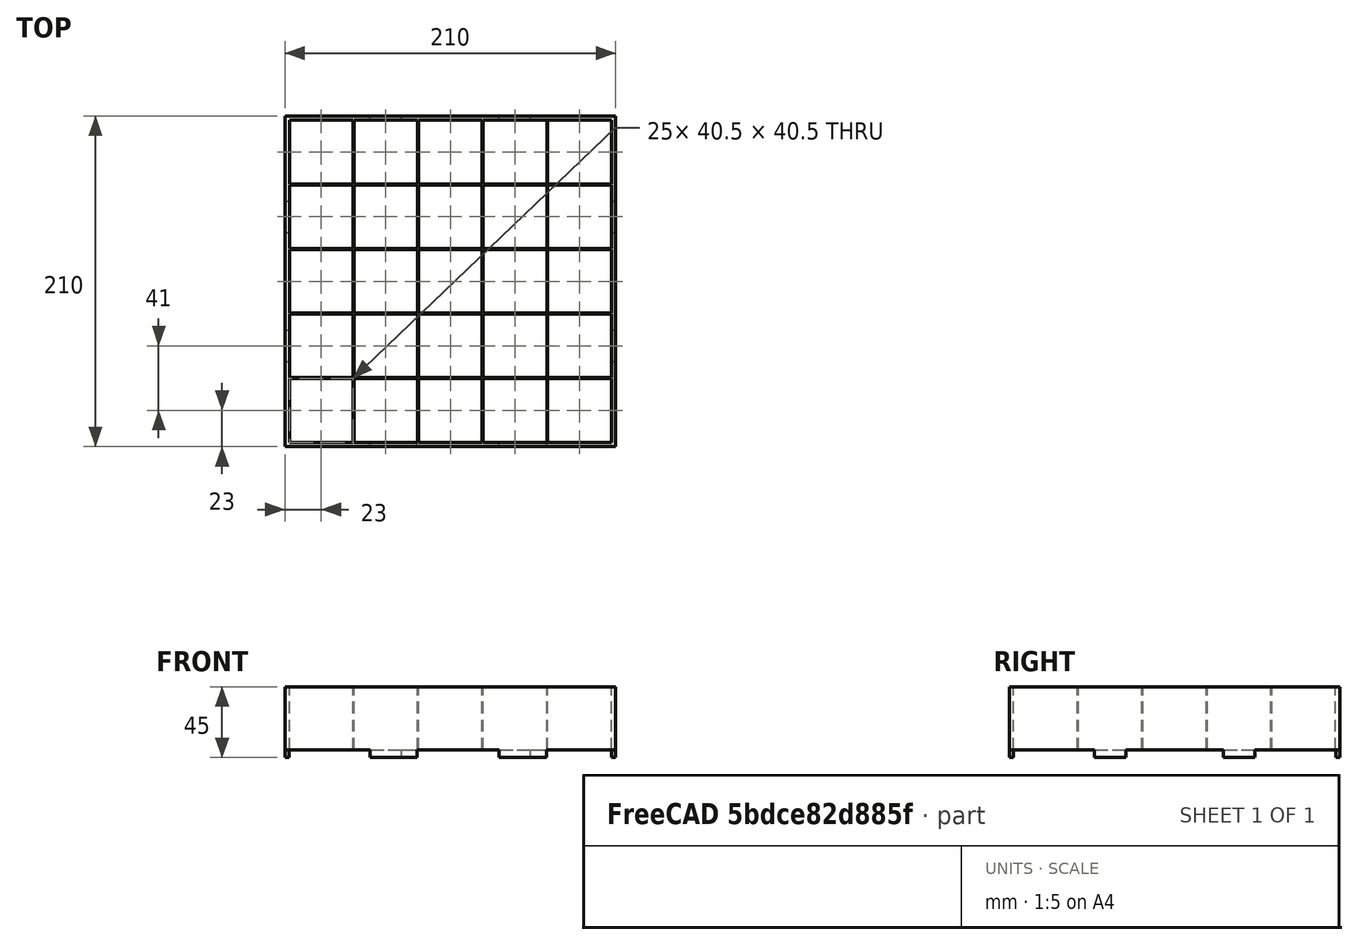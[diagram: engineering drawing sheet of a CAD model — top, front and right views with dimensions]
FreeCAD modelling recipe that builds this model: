
FCSTD DOCUMENT  (FreeCAD 0.20R29410 (Git))
Label: Ledwall_diffuser_mounting_frame
License: All rights reserved
LicenseURL: http://en.wikipedia.org/wiki/All_rights_reserved
objects: Part::Plane×34, Part::MultiFuse×8, Part::FeaturePython×2, Part::Extrusion×2, Part::Fuse×2, Part::Cut×1
note: 49 computed .brp shape members not serialized (recipe doc carries the construction recipe); baked Part::Feature solids carry a one-line shape summary decoded from their .brp

FEATURE [Part::Plane] square
  AttacherType = Attacher::AttachEngine3D
  Length = 210
  Placement = pos=(-105,-105,0) rot=(0,0,1;0rad)
  Width = 210
FEATURE [Part::Plane] square001 .. square005  x5 (patterned run collapsed; names and placements below)
  AttacherType = Attacher::AttachEngine3D
  Length = 40.5
  Width = 40.5
  placements: 5 in arithmetic series — first pos=(-102.25,-102.25,0) rot=(0,0,1;0rad), step (0,41,0), last pos=(-102.25,61.75,0) rot=(0,0,1;0rad)
FEATURE [Part::MultiFuse] Group
  Shapes = -> [square001,square002,square003,square004,square005]
FEATURE [Part::Plane] square006 .. square010  x5 (patterned run collapsed; names and placements below)
  AttacherType = Attacher::AttachEngine3D
  Length = 40.5
  Width = 40.5
  placements: 5 in arithmetic series — first pos=(-61.25,-102.25,0) rot=(0,0,1;0rad), step (0,41,0), last pos=(-61.25,61.75,0) rot=(0,0,1;0rad)
FEATURE [Part::MultiFuse] Group001
  Shapes = -> [square006,square007,square008,square009,square010]
FEATURE [Part::Plane] square011 .. square015  x5 (patterned run collapsed; names and placements below)
  AttacherType = Attacher::AttachEngine3D
  Length = 40.5
  Width = 40.5
  placements: 5 in arithmetic series — first pos=(-20.25,-102.25,0) rot=(0,0,1;0rad), step (0,41,0), last pos=(-20.25,61.75,0) rot=(0,0,1;0rad)
FEATURE [Part::MultiFuse] Group002
  Shapes = -> [square011,square012,square013,square014,square015]
FEATURE [Part::Plane] square016 .. square020  x5 (patterned run collapsed; names and placements below)
  AttacherType = Attacher::AttachEngine3D
  Length = 40.5
  Width = 40.5
  placements: 5 in arithmetic series — first pos=(20.75,-102.25,0) rot=(0,0,1;0rad), step (0,41,0), last pos=(20.75,61.75,0) rot=(0,0,1;0rad)
FEATURE [Part::MultiFuse] Group003
  Shapes = -> [square016,square017,square018,square019,square020]
FEATURE [Part::Plane] square021 .. square025  x5 (patterned run collapsed; names and placements below)
  AttacherType = Attacher::AttachEngine3D
  Length = 40.5
  Width = 40.5
  placements: 5 in arithmetic series — first pos=(61.75,-102.25,0) rot=(0,0,1;0rad), step (0,41,0), last pos=(61.75,61.75,0) rot=(0,0,1;0rad)
FEATURE [Part::MultiFuse] Group004
  Shapes = -> [square021,square022,square023,square024,square025]
FEATURE [Part::MultiFuse] Group005
  Shapes = -> [Group,Group001,Group002,Group003,Group004]
FEATURE [Part::Cut] difference
  Base = -> square
  Tool = -> Group005
FEATURE [Part::FeaturePython] RefineLinearExtrude  # WARN: FeaturePython — macro-defined, semantics opaque (R4)
  Base = -> difference
FEATURE [Part::Extrusion] LinearExtrude
  Base = -> RefineLinearExtrude
  Dir = (0,0,40)
  DirMode = 0
  FaceMakerClass = Part::FaceMakerBullseye
  LengthFwd = 0
  LengthRev = 0
  Placement = pos=(0,0,-20) rot=(0,0,1;0rad)
  Solid = false
  Symmetric = false
FEATURE [Part::Plane] square026
  AttacherType = Attacher::AttachEngine3D
  Length = 30
  Placement = pos=(-51,-105,0) rot=(0,0,1;0rad)
  Width = 2.5
FEATURE [Part::Plane] square027
  AttacherType = Attacher::AttachEngine3D
  Length = 2.5
  Placement = pos=(-105,-51,0) rot=(0,0,1;0rad)
  Width = 20
FEATURE [Part::Plane] square028
  AttacherType = Attacher::AttachEngine3D
  Length = 20
  Placement = pos=(-51,102.5,0) rot=(0,0,1;0rad)
  Width = 2.5
FEATURE [Part::Plane] square029
  AttacherType = Attacher::AttachEngine3D
  Length = 2.5
  Placement = pos=(-105,31,0) rot=(0,0,1;0rad)
  Width = 20
FEATURE [Part::MultiFuse] Group006
  Shapes = -> [square026,square027,square028,square029]
FEATURE [Part::Plane] square030
  AttacherType = Attacher::AttachEngine3D
  Length = 30
  Placement = pos=(31,-105,0) rot=(0,0,1;0rad)
  Width = 2.5
FEATURE [Part::Plane] square031
  AttacherType = Attacher::AttachEngine3D
  Length = 2.5
  Placement = pos=(102.5,-51,0) rot=(0,0,1;0rad)
  Width = 20
FEATURE [Part::Plane] square032
  AttacherType = Attacher::AttachEngine3D
  Length = 20
  Placement = pos=(31,102.5,0) rot=(0,0,1;0rad)
  Width = 2.5
FEATURE [Part::Plane] square033
  AttacherType = Attacher::AttachEngine3D
  Length = 2.5
  Placement = pos=(102.5,31,0) rot=(0,0,1;0rad)
  Width = 20
FEATURE [Part::MultiFuse] Group007
  Shapes = -> [square030,square031,square032,square033]
FEATURE [Part::Fuse] Group008
  Base = -> Group006
  Tool = -> Group007
FEATURE [Part::FeaturePython] RefineLinearExtrude001  # WARN: FeaturePython — macro-defined, semantics opaque (R4)
  Base = -> Group008
FEATURE [Part::Extrusion] LinearExtrude001
  Base = -> RefineLinearExtrude001
  Dir = (0,0,5)
  DirMode = 0
  FaceMakerClass = Part::FaceMakerBullseye
  LengthFwd = 0
  LengthRev = 0
  Placement = pos=(0,0,-25) rot=(0,0,1;0rad)
  Solid = false
  Symmetric = false
FEATURE [Part::Fuse] union
  Base = -> LinearExtrude
  Tool = -> LinearExtrude001
